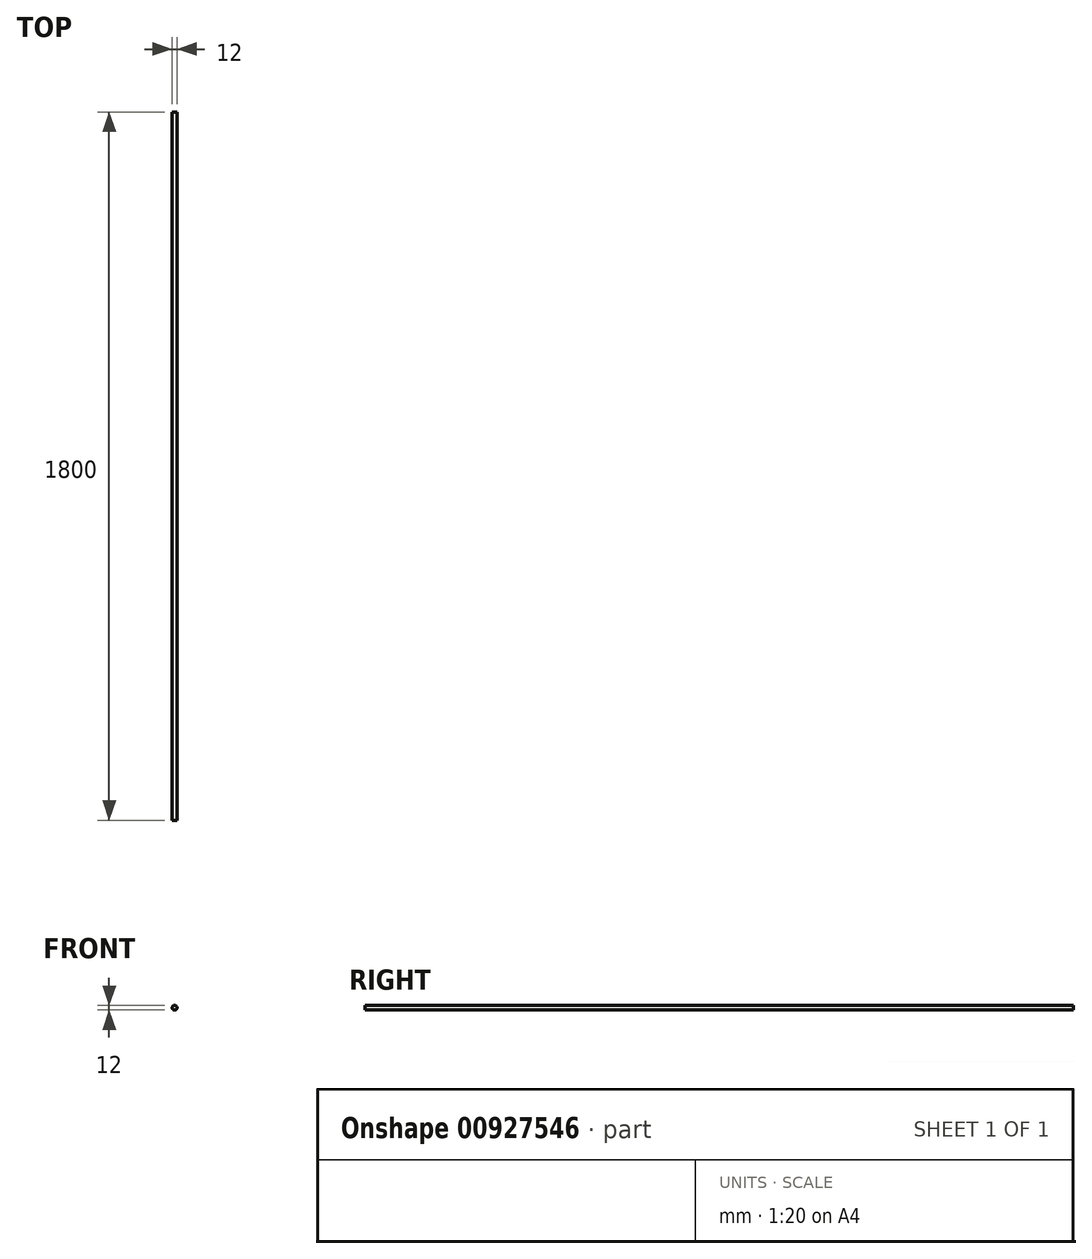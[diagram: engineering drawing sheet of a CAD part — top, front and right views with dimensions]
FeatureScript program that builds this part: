
annotation { "Feature Type Name" : "Feature", "Feature Type Description" : "" }
export const myFeature = defineFeature(function(context is Context, id is Id, definition is map)
    precondition{}
    {
        {
            var Q0;
            Q0=qCreatedBy(makeId("Front.planeOp"),FACE);
            var sketch = newSketch(context, id + "F0", { "sketchPlane" : qUnion([Q0])});
            skCircle(sketch, "E0", {"center": v(0, 0) * mm, "radius": 6 * mm});
            skSolve(sketch);
        }
        {
            var Q0;
            Q0=makeQuery(id+"F0.imprint","IMPRINT",FACE,{"disambiguationData":[TD([[makeQuery(id+"F0.imprint","IMPRINT",EDGE,{"derivedFrom":sQuery(id+"F0.wireOp",EDGE,"E0")}),1.0]])]});
            extrude(context, id + "F1", {"entities" : qUnion([Q0]), "depth" : 1800 * mm, "offsetDistance" : 25 * mm});
        }
    });
